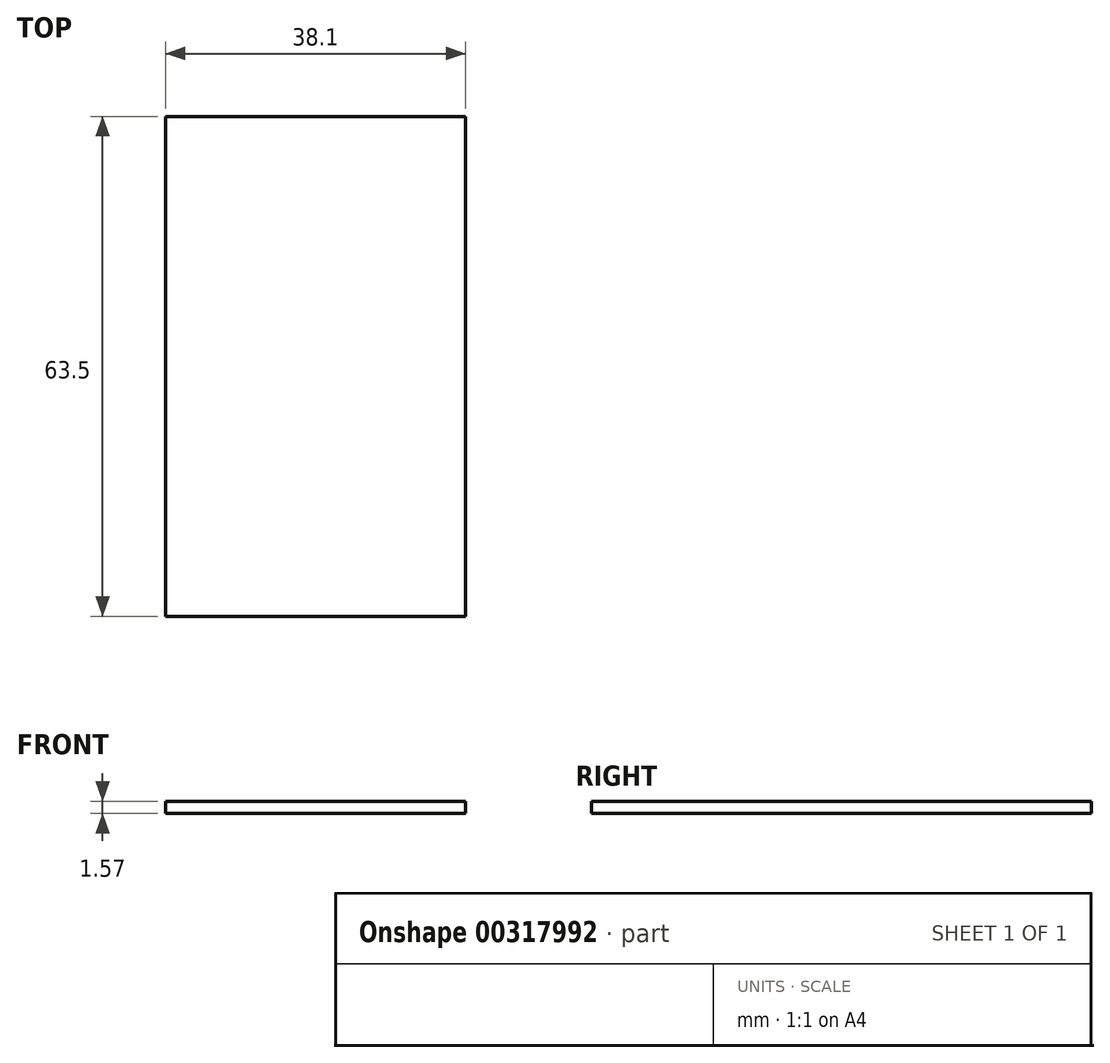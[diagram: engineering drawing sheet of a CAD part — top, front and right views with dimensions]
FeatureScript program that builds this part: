
annotation { "Feature Type Name" : "Feature", "Feature Type Description" : "" }
export const myFeature = defineFeature(function(context is Context, id is Id, definition is map)
    precondition{}
    {
        {
            var Q0;
            Q0=qCreatedBy(makeId("Top.planeOp"),FACE);
            var sketch = newSketch(context, id + "F0", { "sketchPlane" : qUnion([Q0])});
            skLineSegment(sketch, "E0.bottom", {"start": v(0, 0) * mm, "end": v(38.1, 0) * mm});
            skLineSegment(sketch, "E0.top", {"start": v(0, 63.5) * mm, "end": v(38.1, 63.5) * mm});
            skLineSegment(sketch, "E0.left", {"start": v(0, 0) * mm, "end": v(0, 63.5) * mm});
            skLineSegment(sketch, "E0.right", {"start": v(38.1, 0) * mm, "end": v(38.1, 63.5) * mm});
            skSolve(sketch);
        }
        {
            var Q0;
            Q0=makeQuery(id+"F0.imprint","IMPRINT",FACE,{"disambiguationData":[TD([[makeQuery(id+"F0.imprint","IMPRINT",EDGE,{"derivedFrom":sQuery(id+"F0.wireOp",EDGE,"E0.bottom")}),1.0]])]});
            extrude(context, id + "F1", {"entities" : qUnion([Q0]), "depth" : 1.57 * mm});
        }
    });
